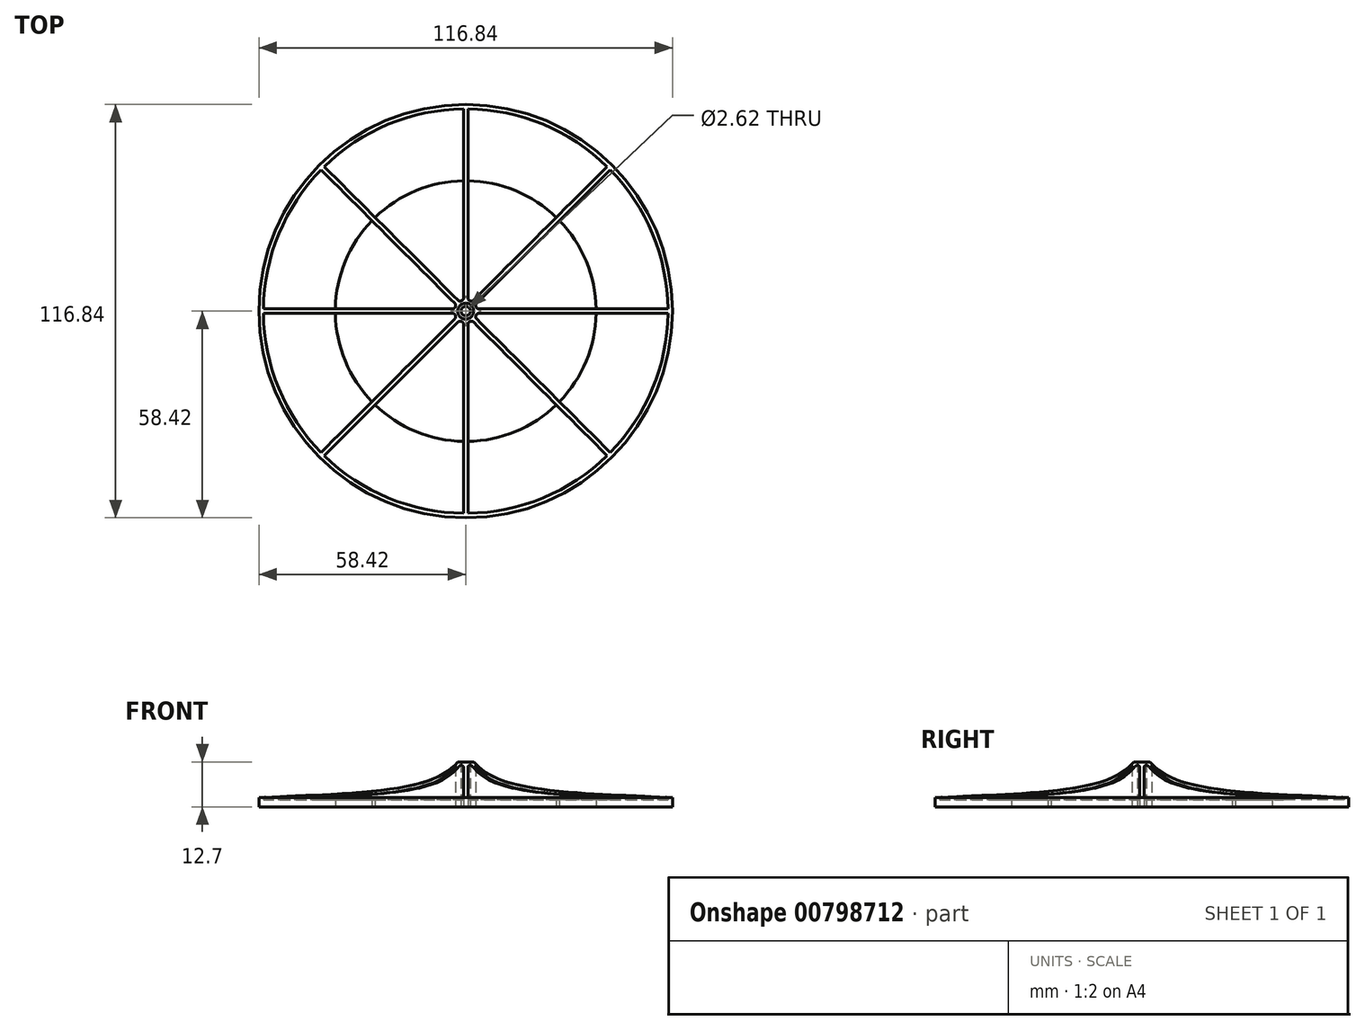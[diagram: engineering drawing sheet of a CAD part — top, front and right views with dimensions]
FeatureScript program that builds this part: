
annotation { "Feature Type Name" : "Feature", "Feature Type Description" : "" }
export const myFeature = defineFeature(function(context is Context, id is Id, definition is map)
    precondition{}
    {
        {
            var Q0;
            Q0=qCreatedBy(makeId("Top.planeOp"),FACE);
            var sketch = newSketch(context, id + "F0", { "sketchPlane" : qUnion([Q0])});
            skCircle(sketch, "E0", {"center": v(0, 0) * mm, "radius": 58.42 * mm});
            skArc(sketch, "E1", {"start": v(-57.15, -0.63) * mm, "mid": v(-52.8, -21.87) * mm, "end": v(-40.86, -39.96) * mm});
            skArc(sketch, "E2", {"start": v(-2.9, 1.3) * mm, "mid": v(-2.93, 1.22) * mm, "end": v(-2.97, 1.13) * mm});
            skLineSegment(sketch, "E3.left", {"start": v(0, 3.17) * mm, "end": v(0, 3.11) * mm});
            skLineSegment(sketch, "E3.right", {"start": v(0.64, 57.15) * mm, "end": v(0.64, 38.1) * mm});
            skLineSegment(sketch, "E4.MirrorCS", {"start": v(-0.64, 57.15) * mm, "end": v(-0.64, 39.36) * mm});
            skLineSegment(sketch, "E5.1.0", {"start": v(-39.96, 40.86) * mm, "end": v(-26.49, 27.39) * mm});
            skLineSegment(sketch, "E5.1.1", {"start": v(-40.86, 39.96) * mm, "end": v(-27.39, 26.49) * mm});
            skLineSegment(sketch, "E5.2.0", {"start": v(-57.15, 0.64) * mm, "end": v(-38.1, 0.64) * mm});
            skLineSegment(sketch, "E5.2.1", {"start": v(-57.15, -0.64) * mm, "end": v(-39.36, -0.64) * mm});
            skLineSegment(sketch, "E5.3.0", {"start": v(-40.86, -39.96) * mm, "end": v(-27.39, -26.49) * mm});
            skLineSegment(sketch, "E5.3.1", {"start": v(-39.96, -40.86) * mm, "end": v(-27.39, -28.28) * mm});
            skLineSegment(sketch, "E5.4.0", {"start": v(-0.64, -57.15) * mm, "end": v(-0.64, -38.1) * mm});
            skLineSegment(sketch, "E5.4.1", {"start": v(0.63, -57.15) * mm, "end": v(0.63, -39.36) * mm});
            skLineSegment(sketch, "E5.5.0", {"start": v(39.96, -40.86) * mm, "end": v(27.39, -28.28) * mm});
            skLineSegment(sketch, "E5.5.1", {"start": v(40.86, -39.96) * mm, "end": v(27.39, -26.49) * mm});
            skLineSegment(sketch, "E5.6.0", {"start": v(57.15, -0.64) * mm, "end": v(38.1, -0.64) * mm});
            skLineSegment(sketch, "E5.6.1", {"start": v(57.15, 0.63) * mm, "end": v(39.36, 0.63) * mm});
            skLineSegment(sketch, "E5.7.0", {"start": v(40.86, 39.96) * mm, "end": v(28.28, 27.39) * mm});
            skLineSegment(sketch, "E5.7.1", {"start": v(39.96, 40.86) * mm, "end": v(26.49, 27.39) * mm});
            skArc(sketch, "E6.trimOffspring", {"start": v(-39.96, -40.86) * mm, "mid": v(-21.87, -52.8) * mm, "end": v(-0.64, -57.15) * mm});
            skArc(sketch, "E7.trimOffspring", {"start": v(0.63, -57.15) * mm, "mid": v(21.87, -52.8) * mm, "end": v(39.96, -40.86) * mm});
            skArc(sketch, "E8.trimOffspring", {"start": v(40.86, -39.96) * mm, "mid": v(52.8, -21.87) * mm, "end": v(57.15, -0.64) * mm});
            skArc(sketch, "E9.trimOffspring", {"start": v(57.15, 0.64) * mm, "mid": v(52.8, 21.87) * mm, "end": v(40.86, 39.96) * mm});
            skArc(sketch, "E10.trimOffspring", {"start": v(39.96, 40.86) * mm, "mid": v(21.87, 52.8) * mm, "end": v(0.64, 57.15) * mm});
            skArc(sketch, "E11.trimOffspring", {"start": v(-0.64, 57.15) * mm, "mid": v(-21.87, 52.8) * mm, "end": v(-39.96, 40.86) * mm});
            skPoint(sketch, "E12.orphan", {"position": v(0, 57.15) * mm});
            skArc(sketch, "E13.trimOffspring", {"start": v(-40.86, 39.96) * mm, "mid": v(-52.8, 21.87) * mm, "end": v(-57.15, 0.64) * mm});
            skArc(sketch, "E14.trimOffspring", {"start": v(-2.97, -1.13) * mm, "mid": v(-2.93, -1.22) * mm, "end": v(-2.9, -1.3) * mm});
            skArc(sketch, "E15.trimOffspring", {"start": v(-1.3, -2.9) * mm, "mid": v(-1.22, -2.93) * mm, "end": v(-1.13, -2.97) * mm});
            skArc(sketch, "E16.trimOffspring", {"start": v(1.13, -2.97) * mm, "mid": v(1.22, -2.93) * mm, "end": v(1.3, -2.9) * mm});
            skArc(sketch, "E17.trimOffspring", {"start": v(2.9, -1.3) * mm, "mid": v(2.93, -1.22) * mm, "end": v(2.97, -1.13) * mm});
            skArc(sketch, "E18.trimOffspring", {"start": v(2.97, 1.13) * mm, "mid": v(2.93, 1.22) * mm, "end": v(2.9, 1.3) * mm});
            skArc(sketch, "E19.trimOffspring", {"start": v(1.3, 2.9) * mm, "mid": v(1.22, 2.93) * mm, "end": v(1.13, 2.97) * mm});
            skArc(sketch, "E20.trimOffspring", {"start": v(-1.13, 2.97) * mm, "mid": v(-1.22, 2.93) * mm, "end": v(-1.3, 2.9) * mm});
            skPoint(sketch, "E21.visualSharp", {"position": v(-2.65, 1.75) * mm});
            skArc(sketch, "E21.filletArc", {"start": v(-2.9, 1.3) * mm, "mid": v(-2.84, 1.75) * mm, "end": v(-3.05, 2.15) * mm});
            skPoint(sketch, "E22.visualSharp", {"position": v(-3.11, 0.64) * mm});
            skArc(sketch, "E22.filletArc", {"start": v(-3.68, 0.64) * mm, "mid": v(-3.25, 0.77) * mm, "end": v(-2.97, 1.13) * mm});
            skPoint(sketch, "E23.visualSharp", {"position": v(-3.11, -0.64) * mm});
            skArc(sketch, "E23.filletArc", {"start": v(-2.97, -1.13) * mm, "mid": v(-3.25, -0.77) * mm, "end": v(-3.68, -0.64) * mm});
            skPoint(sketch, "E24.visualSharp", {"position": v(-2.65, -1.75) * mm});
            skArc(sketch, "E24.filletArc", {"start": v(-3.05, -2.15) * mm, "mid": v(-2.84, -1.75) * mm, "end": v(-2.9, -1.3) * mm});
            skPoint(sketch, "E25.visualSharp", {"position": v(-1.75, -2.65) * mm});
            skArc(sketch, "E25.filletArc", {"start": v(-1.3, -2.9) * mm, "mid": v(-1.75, -2.84) * mm, "end": v(-2.15, -3.05) * mm});
            skPoint(sketch, "E26.visualSharp", {"position": v(-0.64, -3.11) * mm});
            skArc(sketch, "E26.filletArc", {"start": v(-0.64, -3.68) * mm, "mid": v(-0.77, -3.25) * mm, "end": v(-1.13, -2.97) * mm});
            skPoint(sketch, "E27.visualSharp", {"position": v(0.64, -3.11) * mm});
            skArc(sketch, "E27.filletArc", {"start": v(1.13, -2.97) * mm, "mid": v(0.77, -3.25) * mm, "end": v(0.64, -3.68) * mm});
            skPoint(sketch, "E28.visualSharp", {"position": v(1.75, -2.65) * mm});
            skArc(sketch, "E28.filletArc", {"start": v(2.15, -3.05) * mm, "mid": v(1.75, -2.84) * mm, "end": v(1.3, -2.9) * mm});
            skPoint(sketch, "E29.visualSharp", {"position": v(2.65, -1.75) * mm});
            skArc(sketch, "E29.filletArc", {"start": v(2.9, -1.3) * mm, "mid": v(2.84, -1.75) * mm, "end": v(3.05, -2.15) * mm});
            skPoint(sketch, "E30.visualSharp", {"position": v(3.11, -0.64) * mm});
            skArc(sketch, "E30.filletArc", {"start": v(3.68, -0.64) * mm, "mid": v(3.25, -0.77) * mm, "end": v(2.97, -1.13) * mm});
            skPoint(sketch, "E31.visualSharp", {"position": v(3.11, 0.64) * mm});
            skArc(sketch, "E31.filletArc", {"start": v(2.97, 1.13) * mm, "mid": v(3.25, 0.77) * mm, "end": v(3.68, 0.64) * mm});
            skPoint(sketch, "E32.visualSharp", {"position": v(2.65, 1.75) * mm});
            skArc(sketch, "E32.filletArc", {"start": v(3.05, 2.15) * mm, "mid": v(2.84, 1.75) * mm, "end": v(2.9, 1.3) * mm});
            skPoint(sketch, "E33.visualSharp", {"position": v(1.75, 2.65) * mm});
            skArc(sketch, "E33.filletArc", {"start": v(1.3, 2.9) * mm, "mid": v(1.75, 2.84) * mm, "end": v(2.15, 3.05) * mm});
            skPoint(sketch, "E34.visualSharp", {"position": v(0.64, 3.11) * mm});
            skArc(sketch, "E34.filletArc", {"start": v(0.64, 3.68) * mm, "mid": v(0.77, 3.25) * mm, "end": v(1.13, 2.97) * mm});
            skPoint(sketch, "E35.visualSharp", {"position": v(-0.64, 3.11) * mm});
            skArc(sketch, "E35.filletArc", {"start": v(-1.13, 2.97) * mm, "mid": v(-0.77, 3.25) * mm, "end": v(-0.64, 3.68) * mm});
            skPoint(sketch, "E36.visualSharp", {"position": v(-1.75, 2.65) * mm});
            skArc(sketch, "E36.filletArc", {"start": v(-2.15, 3.05) * mm, "mid": v(-1.75, 2.84) * mm, "end": v(-1.3, 2.9) * mm});
            skCircle(sketch, "E37", {"center": v(0, 0) * mm, "radius": 1.3 * mm});
            skLineSegment(sketch, "E38.trimOffspring", {"start": v(26.49, 27.39) * mm, "end": v(2.15, 3.05) * mm});
            skLineSegment(sketch, "E39.trimOffspring", {"start": v(28.28, 27.39) * mm, "end": v(3.05, 2.15) * mm});
            skLineSegment(sketch, "E40.trimOffspring", {"start": v(39.36, 0.63) * mm, "end": v(3.68, 0.64) * mm});
            skLineSegment(sketch, "E41.trimOffspring", {"start": v(38.1, -0.64) * mm, "end": v(3.68, -0.64) * mm});
            skLineSegment(sketch, "E42.trimOffspring", {"start": v(-26.49, 27.39) * mm, "end": v(-2.15, 3.05) * mm});
            skLineSegment(sketch, "E43.trimOffspring", {"start": v(-27.39, 26.49) * mm, "end": v(-3.05, 2.15) * mm});
            skLineSegment(sketch, "E44.trimOffspring", {"start": v(-0.64, 39.36) * mm, "end": v(-0.64, 3.68) * mm});
            skLineSegment(sketch, "E45.trimOffspring", {"start": v(0.64, 38.1) * mm, "end": v(0.64, 3.68) * mm});
            skLineSegment(sketch, "E46.trimOffspring", {"start": v(-39.36, -0.64) * mm, "end": v(-3.68, -0.64) * mm});
            skLineSegment(sketch, "E47.trimOffspring", {"start": v(-38.1, 0.64) * mm, "end": v(-3.68, 0.64) * mm});
            skLineSegment(sketch, "E48.trimOffspring", {"start": v(-27.39, -26.49) * mm, "end": v(-3.05, -2.15) * mm});
            skLineSegment(sketch, "E49.trimOffspring", {"start": v(-27.39, -28.28) * mm, "end": v(-2.15, -3.05) * mm});
            skLineSegment(sketch, "E50.trimOffspring", {"start": v(-0.64, -38.1) * mm, "end": v(-0.64, -3.68) * mm});
            skLineSegment(sketch, "E51.trimOffspring", {"start": v(0.63, -39.36) * mm, "end": v(0.64, -3.68) * mm});
            skLineSegment(sketch, "E52.trimOffspring", {"start": v(27.39, -26.49) * mm, "end": v(3.05, -2.15) * mm});
            skLineSegment(sketch, "E53.trimOffspring", {"start": v(27.39, -28.28) * mm, "end": v(2.15, -3.05) * mm});
            skSolve(sketch);
        }
        {
            var Q0;
            Q0=makeQuery(id+"F0.imprint","IMPRINT",FACE,{"disambiguationData":[TD([[makeQuery(id+"F0.imprint","IMPRINT",EDGE,{"derivedFrom":sQuery(id+"F0.wireOp",EDGE,"E0")}),1.0]])]});
            extrude(context, id + "F1", {"entities" : qUnion([Q0]), "depth" : 12.7 * mm, "offsetDistance" : 25.4 * mm});
        }
        {
            var Q0;
            Q0=qCreatedBy(makeId("Top.planeOp"),FACE);
            var sketch = newSketch(context, id + "F2", { "sketchPlane" : qUnion([Q0])});
            skCircle(sketch, "E54", {"center": v(0, 0) * mm, "radius": 58.42 * mm});
            skCircle(sketch, "E55", {"center": v(0, 0) * mm, "radius": 36.83 * mm});
            skSolve(sketch);
        }
        {
            var Q0;
            Q0 = qSketchRegion(id + "F2", true);
            extrude(context, id + "F3", {"entities" : qUnion([Q0]), "operationType" : NewBodyOperationType.ADD, "depth" : 2 * mm, "offsetDistance" : 25.4 * mm});
        }
        {
            var Q0;
            Q0=qCreatedBy(makeId("Right.planeOp"),FACE);
            var sketch = newSketch(context, id + "F4", { "sketchPlane" : qUnion([Q0])});
            skLineSegment(sketch, "E56.bottom", {"start": v(0, 24.07) * mm, "end": v(63.28, 24.07) * mm});
            skLineSegment(sketch, "E56.left", {"start": v(0, 24.07) * mm, "end": v(0, 16.63) * mm});
            skLineSegment(sketch, "E56.right", {"start": v(63.28, 24.07) * mm, "end": v(63.28, 0) * mm});
            skPoint(sketch, "E56.top.start.orphan", {"position": v(0, 9.19) * mm});
            skFitSpline(sketch, "E57", {"points": [v(0, 16.63) * mm, v(14.09, 6.32) * mm, v(61.87, 2.1) * mm, v(63.28, 0) * mm], "startDerivative": vector(15.3, -40.46) * mm, "endDerivative": vector(6.2, -33.31) * mm});
            skSolve(sketch);
        }
        {
            var Q0;
            Q0=makeQuery(id+"F4.imprint","IMPRINT",FACE,{"disambiguationData":[TD([[makeQuery(id+"F4.imprint","IMPRINT",EDGE,{"derivedFrom":sQuery(id+"F4.wireOp",EDGE,"T3sZDioS-9toB-0m7N-Xn5q-EQyuKV1LG3Li.bottom")}),-1.0]])]});
            var Q1;
            Q1=makeQuery(id+"F4.imprint","IMPRINT",FACE,{"disambiguationData":[TD([[makeQuery(id+"F4.imprint","IMPRINT",EDGE,{"derivedFrom":sQuery(id+"F4.wireOp",EDGE,"E56.bottom")}),-1.0]])]});
            var Q2;
            Q2=makeQuery(id+"F1.opExtrude","SWEPT_FACE",FACE,{"disambiguationData":[OSD([sQuery(id+"F0.wireOp",EDGE,"E0")])]});
            revolve(context, id + "F5", {"operationType" : NewBodyOperationType.REMOVE, "surfaceOperationType" : NewSurfaceOperationType.NEW, "entities" : qUnion([Q0, Q1]), "axis" : qUnion([Q2]), "revolveType" : RevolveType.FULL, "oppositeDirection" : true});
        }
    });
